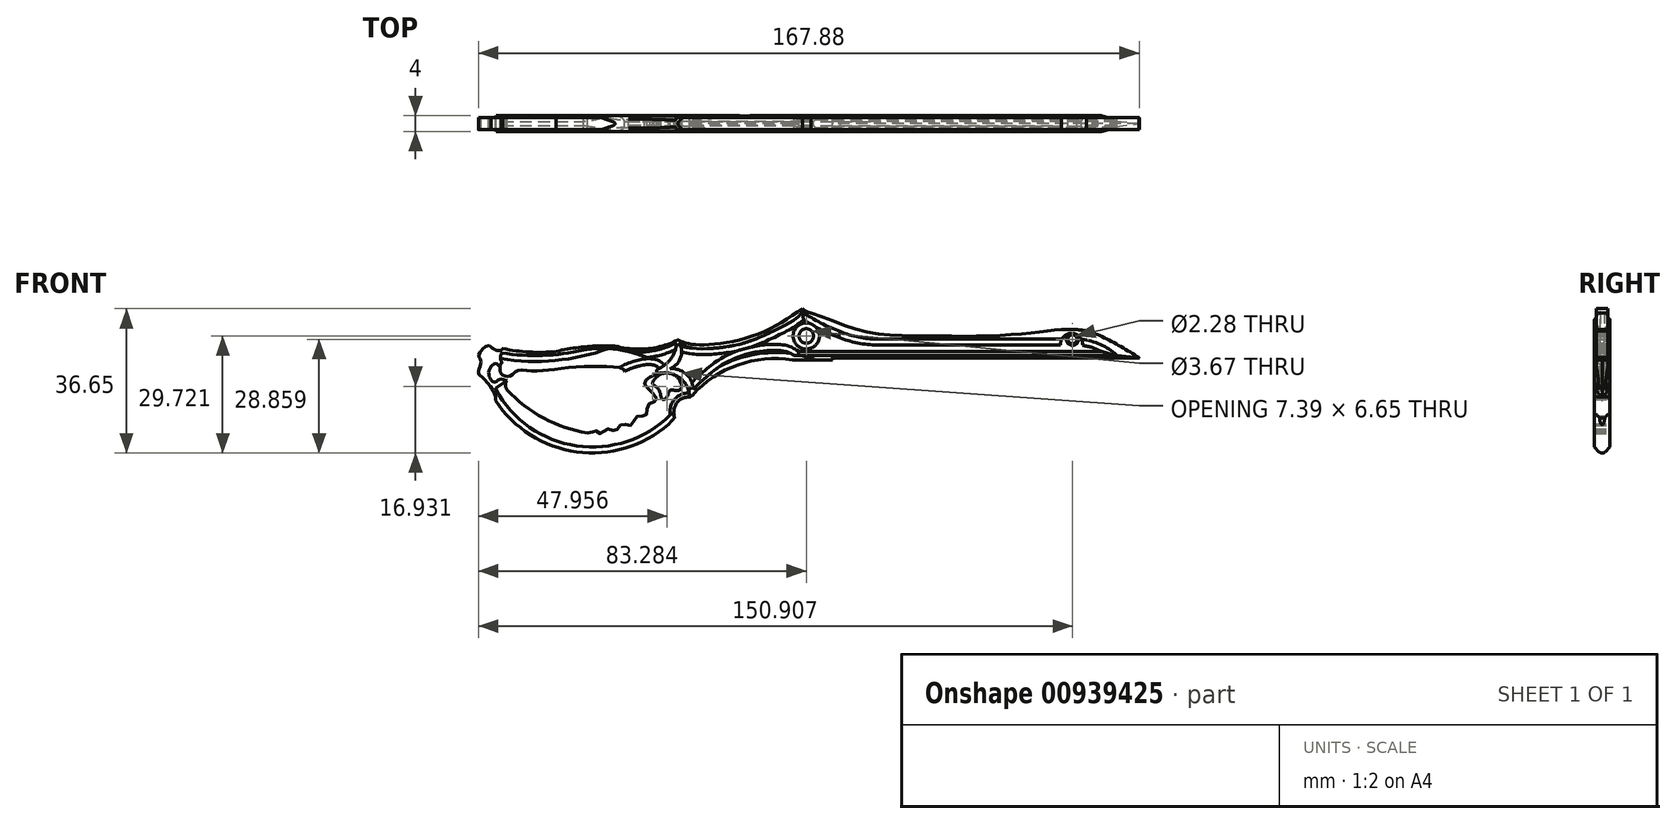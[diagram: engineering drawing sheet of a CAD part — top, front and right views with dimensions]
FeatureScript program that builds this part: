
annotation { "Feature Type Name" : "Feature", "Feature Type Description" : "" }
export const myFeature = defineFeature(function(context is Context, id is Id, definition is map)
    precondition{}
    {
        {
            var Q0;
            Q0=qCreatedBy(makeId("Front.planeOp"),FACE);
            var sketch = newSketch(context, id + "F0", { "sketchPlane" : qUnion([Q0])});
            skLineSegment(sketch, "E0", {"start": v(-6.71, -12.54) * mm, "end": v(71.27, -12.54) * mm});
            skCircle(sketch, "E1", {"center": v(-13.33, -6.93) * mm, "radius": 1.84 * mm});
            skFitSpline(sketch, "E2", {"points": [v(-12.11, -1.12) * mm, v(-13.61, -0.53) * mm, v(-14.23, 0) * mm, v(-14.23, 0) * mm], "startDerivative": vector(-2.76, 0.75) * mm, "endDerivative": vector(0.22, -0.06) * mm});
            skFitSpline(sketch, "E3", {"points": [v(-14.23, 0) * mm, v(-26.09, -6.66) * mm, v(-38.83, -9.19) * mm, v(-43.7, -8.8) * mm, v(-46, -7.9) * mm, v(-48, -6.13) * mm, v(-48.96, -3.93) * mm], "startDerivative": vector(-43.16, -29.04) * mm, "endDerivative": vector(-6.66, 21.05) * mm});
            skLineSegment(sketch, "E4", {"start": v(65.55, -11.87) * mm, "end": v(-6.71, -11.87) * mm});
            skLineSegment(sketch, "E5", {"start": v(65.55, -11.87) * mm, "end": v(71.27, -12.54) * mm});
            skArc(sketch, "E6", {"start": v(51.62, -7.72) * mm, "mid": v(54.08, -9.28) * mm, "end": v(56.59, -7.8) * mm});
            skArc(sketch, "E7", {"start": v(56.59, -7.8) * mm, "mid": v(54.12, -6.27) * mm, "end": v(51.62, -7.72) * mm});
            skArc(sketch, "E8", {"start": v(65.55, -11.87) * mm, "mid": v(61.4, -9.09) * mm, "end": v(56.59, -7.8) * mm});
            skLineSegment(sketch, "E9", {"start": v(4.84, -7.72) * mm, "end": v(51.62, -7.72) * mm});
            skFitSpline(sketch, "E10", {"points": [v(71.2, -12.47) * mm, v(58.32, -5.78) * mm, v(51.1, -5.34) * mm, v(45.14, -5.98) * mm, v(33.56, -6.92) * mm, v(17.3, -6.92) * mm, v(1.97, -5.9) * mm, v(-12.11, -1.12) * mm], "startDerivative": vector(-75.63, 47.6) * mm, "endDerivative": vector(-90.27, 29.28) * mm});
            skArc(sketch, "E11", {"start": v(71.27, -12.54) * mm, "mid": v(62.17, -6.83) * mm, "end": v(51.53, -5.3) * mm});
            skArc(sketch, "E12", {"start": v(-4.67, -5.85) * mm, "mid": v(0, -7.25) * mm, "end": v(4.84, -7.72) * mm});
            skArc(sketch, "E13", {"start": v(-4.67, -5.85) * mm, "mid": v(-6.16, -9.29) * mm, "end": v(-6.71, -13) * mm});
            skCircle(sketch, "E14", {"center": v(-13.33, -6.93) * mm, "radius": 3 * mm});
            skLineSegment(sketch, "E15", {"start": v(-14.23, 0) * mm, "end": v(-14.34, -0.83) * mm});
            skArc(sketch, "E16", {"start": v(-14.34, -0.83) * mm, "mid": v(-9.65, -3.62) * mm, "end": v(-4.67, -5.85) * mm});
            skLineSegment(sketch, "E17", {"start": v(-6.71, -13) * mm, "end": v(-16.86, -13) * mm});
            skArc(sketch, "E18", {"start": v(-16.86, -13) * mm, "mid": v(-16.58, -12.45) * mm, "end": v(-16.49, -11.84) * mm});
            skFitSpline(sketch, "E19", {"points": [v(-16.49, -11.84) * mm, v(-18.47, -10.89) * mm, v(-24.7, -10.8) * mm, v(-32.93, -13.26) * mm, v(-38.38, -17.07) * mm, v(-42.08, -20.53) * mm], "startDerivative": vector(-13.57, 7.8) * mm, "endDerivative": vector(-16.57, -17.02) * mm});
            skPoint(sketch, "E20", {"position": v(-47.93, -15.27) * mm});
            skArc(sketch, "E21", {"start": v(-47.93, -15.27) * mm, "mid": v(-45.1, -11.92) * mm, "end": v(-46.31, -7.7) * mm});
            skArc(sketch, "E22", {"start": v(-42.27, -22) * mm, "mid": v(-43.33, -17.15) * mm, "end": v(-47.93, -15.27) * mm});
            skFitSpline(sketch, "E23", {"points": [v(-14.34, -0.83) * mm, v(-16.03, -2.58) * mm, v(-23.15, -6.4) * mm, v(-30.92, -9.17) * mm, v(-41.48, -10.11) * mm, v(-45.4, -9.05) * mm], "startDerivative": vector(-10.1, -13.37) * mm, "endDerivative": vector(-20.55, 8.32) * mm});
            skFitSpline(sketch, "E24", {"points": [v(-42.36, -10) * mm, v(-43.44, -9.88) * mm, v(-44.44, -9.68) * mm, v(-45.23, -9.5) * mm], "startDerivative": vector(-3.07, 0.24) * mm, "endDerivative": vector(-2.45, 0.6) * mm});
            skLineSegment(sketch, "E25", {"start": v(-6.71, -11.87) * mm, "end": v(-16.49, -11.84) * mm});
            skArc(sketch, "E26", {"start": v(-16.86, -13) * mm, "mid": v(-30.7, -14.28) * mm, "end": v(-42.27, -22) * mm});
            skPoint(sketch, "E27", {"position": v(-90.44, -10.11) * mm});
            skArc(sketch, "E28", {"start": v(-58.53, -9.72) * mm, "mid": v(-52.28, -9.58) * mm, "end": v(-46.31, -7.7) * mm});
            skArc(sketch, "E29", {"start": v(-90.44, -10.11) * mm, "mid": v(-83.7, -11.04) * mm, "end": v(-76.9, -10.87) * mm});
            skArc(sketch, "E30", {"start": v(-90.44, -10.11) * mm, "mid": v(-90.75, -10.64) * mm, "end": v(-90.67, -11.26) * mm});
            skArc(sketch, "E31", {"start": v(-90.67, -11.26) * mm, "mid": v(-80.27, -11.88) * mm, "end": v(-69.94, -10.47) * mm});
            skArc(sketch, "E32", {"start": v(-58.53, -10.87) * mm, "mid": v(-52.52, -10.74) * mm, "end": v(-46.8, -8.86) * mm});
            skArc(sketch, "E33", {"start": v(-50.73, -15.2) * mm, "mid": v(-47.34, -12.15) * mm, "end": v(-46.31, -7.7) * mm});
            skArc(sketch, "E34", {"start": v(-50.73, -15.2) * mm, "mid": v(-51.31, -15.77) * mm, "end": v(-50.86, -16.46) * mm});
            skArc(sketch, "E35", {"start": v(-90.67, -11.26) * mm, "mid": v(-91.02, -12.43) * mm, "end": v(-90.67, -13.6) * mm});
            skLineSegment(sketch, "E36", {"start": v(-42.94, -22.49) * mm, "end": v(-42.27, -22) * mm});
            skPoint(sketch, "E37", {"position": v(-92.52, -22.95) * mm});
            skFitSpline(sketch, "E38", {"points": [v(-90.67, -13.6) * mm, v(-88.53, -14.18) * mm, v(-87.1, -13.28) * mm, v(-85.34, -13.04) * mm, v(-79.56, -13.87) * mm, v(-71.78, -12.97) * mm, v(-65.23, -11.98) * mm, v(-61.23, -11.82) * mm, v(-59.13, -13.12) * mm, v(-52.32, -11.99) * mm, v(-48.92, -13.55) * mm, v(-46.35, -9.28) * mm], "startDerivative": vector(37, -29.54) * mm, "endDerivative": vector(31.14, 31.46) * mm});
            skFitSpline(sketch, "E39", {"points": [v(-50.73, -15.2) * mm, v(-59.56, -15.94) * mm], "startDerivative": vector(-4.3, 5.9) * mm, "endDerivative": vector(-8.43, -4.22) * mm});
            skFitSpline(sketch, "E40", {"points": [v(-59.56, -15.94) * mm, v(-63.38, -14.71) * mm, v(-75.18, -15.14) * mm, v(-82.6, -15.83) * mm, v(-86.83, -15.8) * mm, v(-88.53, -17.16) * mm, v(-89.81, -17.06) * mm, v(-90.91, -16.47) * mm], "startDerivative": vector(-0.92, 20.53) * mm, "endDerivative": vector(-6.34, 15.13) * mm});
            skArc(sketch, "E41", {"start": v(-90.67, -13.6) * mm, "mid": v(-91.16, -15) * mm, "end": v(-90.91, -16.47) * mm});
            skArc(sketch, "E42", {"start": v(-46.35, -9.28) * mm, "mid": v(-46.44, -8.92) * mm, "end": v(-46.8, -8.86) * mm});
            skArc(sketch, "E43", {"start": v(-58.53, -10.87) * mm, "mid": v(-64.22, -10.09) * mm, "end": v(-69.94, -10.47) * mm});
            skArc(sketch, "E44", {"start": v(-58.53, -9.72) * mm, "mid": v(-67.76, -9.55) * mm, "end": v(-76.9, -10.87) * mm});
            skFitSpline(sketch, "E45", {"points": [v(-89.4, -18.28) * mm, v(-91.14, -17.92) * mm, v(-92.48, -18.7) * mm, v(-93.68, -17.64) * mm, v(-93.9, -15.7) * mm, v(-92.6, -14.04) * mm, v(-91.16, -15) * mm], "startDerivative": vector(-14.32, 2.77) * mm, "endDerivative": vector(6.56, -18.2) * mm});
            skArc(sketch, "E46", {"start": v(-42.94, -22.49) * mm, "mid": v(-46.46, -16.98) * mm, "end": v(-52.98, -17.4) * mm});
            skFitSpline(sketch, "E47", {"points": [v(-52.98, -17.4) * mm, v(-54.43, -18.8) * mm, v(-52.7, -21.01) * mm, v(-51.45, -23.34) * mm, v(-53.6, -24.49) * mm, v(-54.04, -27.08) * mm, v(-56.36, -27.4) * mm, v(-57.8, -29.59) * mm, v(-60.18, -29.37) * mm, v(-61.78, -31.07) * mm, v(-64.03, -30.55) * mm, v(-65.67, -31.75) * mm, v(-67.1, -30.95) * mm, v(-68.9, -31.63) * mm], "startDerivative": vector(-16.02, -15.5) * mm, "endDerivative": vector(-36.84, 16.63) * mm});
            skArc(sketch, "E48", {"start": v(-89.34, -20.62) * mm, "mid": v(-80.03, -27.8) * mm, "end": v(-68.9, -31.63) * mm});
            skArc(sketch, "E49", {"start": v(-52.23, -18.52) * mm, "mid": v(-52.33, -19.08) * mm, "end": v(-51.95, -19.5) * mm});
            skArc(sketch, "E50", {"start": v(-50.28, -22.32) * mm, "mid": v(-50.75, -20.7) * mm, "end": v(-51.95, -19.5) * mm});
            skArc(sketch, "E51", {"start": v(-44.96, -19.94) * mm, "mid": v(-48.05, -16.43) * mm, "end": v(-52.23, -18.52) * mm});
            skFitSpline(sketch, "E52", {"points": [v(-44.96, -19.94) * mm, v(-47.73, -20.7) * mm, v(-48.95, -22.74) * mm, v(-50.28, -22.32) * mm], "startDerivative": vector(-4.33, -12.37) * mm, "endDerivative": vector(-2.26, 10.34) * mm});
            skArc(sketch, "E53", {"start": v(-92.3, -23.28) * mm, "mid": v(-71.7, -36.37) * mm, "end": v(-48.3, -29.4) * mm});
            skLineSegment(sketch, "E54", {"start": v(-92.16, -20.16) * mm, "end": v(-92.3, -23.28) * mm});
            skFitSpline(sketch, "E55", {"points": [v(-42.94, -22.49) * mm, v(-46.8, -27.72) * mm], "startDerivative": vector(-7.7, 0.82) * mm, "endDerivative": vector(2.53, -9.45) * mm});
            skLineSegment(sketch, "E56", {"start": v(-46.8, -27.72) * mm, "end": v(-48.3, -29.4) * mm});
            skLineSegment(sketch, "E57", {"start": v(-48.95, -22.74) * mm, "end": v(-49.66, -26.3) * mm});
            skFitSpline(sketch, "E58", {"points": [v(-92.16, -20.16) * mm, v(-78.76, -31.57) * mm, v(-61.25, -33.61) * mm, v(-49.66, -26.3) * mm], "startDerivative": vector(30.49, -37.12) * mm, "endDerivative": vector(21.41, 30.1) * mm});
            skCircle(sketch, "E59", {"center": v(54.3, -7.8) * mm, "radius": 1.14 * mm});
            skArc(sketch, "E60", {"start": v(-89.4, -18.28) * mm, "mid": v(-89.79, -19.46) * mm, "end": v(-89.34, -20.62) * mm});
            skLineSegment(sketch, "E61", {"start": v(-92.16, -20.16) * mm, "end": v(-89.4, -18.28) * mm});
            skFitSpline(sketch, "E62", {"points": [v(-93.37, -9.75) * mm, v(-96.48, -11.66) * mm, v(-96.14, -12.84) * mm, v(-96.16, -14.48) * mm, v(-96.6, -16.4) * mm, v(-95.49, -17.59) * mm, v(-92.28, -22.61) * mm], "startDerivative": vector(-10.84, 18.33) * mm, "endDerivative": vector(-2.51, -11.89) * mm});
            skArc(sketch, "E63", {"start": v(-93.37, -9.75) * mm, "mid": v(-92.17, -10.52) * mm, "end": v(-90.75, -10.64) * mm});
            skSolve(sketch);
        }
        {
            var Q0;
            Q0=makeQuery(id+"F0.imprint","IMPRINT",FACE,{"disambiguationData":[TD([[makeQuery(id+"F0.imprint","IMPRINT",EDGE,{"derivedFrom":sQuery(id+"F0.wireOp",EDGE,"E6")}),-1.0]])]});
            var Q1;
            Q1=makeQuery(id+"F0.imprint","IMPRINT",FACE,{"disambiguationData":[TD([[makeQuery(id+"F0.imprint","IMPRINT",EDGE,{"derivedFrom":sQuery(id+"F0.wireOp",EDGE,"E14")}),-1.0]])]});
            var Q2;
            Q2=makeQuery(id+"F0.imprint","IMPRINT",FACE,{"disambiguationData":[TD([[makeQuery(id+"F0.imprint","IMPRINT",EDGE,{"derivedFrom":sQuery(id+"F0.wireOp",EDGE,"E1")}),-1.0]])]});
            var Q3;
            Q3=makeQuery(id+"F0.imprint","IMPRINT",FACE,{"disambiguationData":[TD([[makeQuery(id+"F0.imprint","IMPRINT",EDGE,{"derivedFrom":sQuery(id+"F0.wireOp",EDGE,"E6")}),1.0]])]});
            var Q4;
            {var subQ8=sQuery(id+"F0.wireOp",EDGE,"E47");Q4=makeQuery(id+"F0.imprint","IMPRINT",FACE,{"disambiguationData":[TD([[makeQuery(id+"F0.imprint","IMPRINT",EDGE,{"derivedFrom":subQ8}),1.0]])]});}
            var Q5;
            Q5=makeQuery(id+"F0.imprint","IMPRINT",FACE,{"disambiguationData":[TD([[makeQuery(id+"F0.imprint","IMPRINT",EDGE,{"derivedFrom":sQuery(id+"F0.wireOp",EDGE,"E31")}),-1.0]])]});
            var Q6;
            {var subQ2=sQuery(id+"F0.wireOp",EDGE,"E38");Q6=makeQuery(id+"F0.imprint","IMPRINT",FACE,{"disambiguationData":[TD([[makeQuery(id+"F0.imprint","IMPRINT",EDGE,{"derivedFrom":subQ2}),-1.0]])]});}
            extrude(context, id + "F1", {"entities" : qUnion([Q0, Q1, Q2, Q3, Q4, Q5, Q6]), "endBound" : BoundingType.SYMMETRIC, "depth" : 4 * mm, "offsetDistance" : 25.4 * mm});
        }
        {
            var Q0;
            Q0=makeQuery(id+"F1.opExtrude","CAP_EDGE",EDGE,{"disambiguationData":[OSD([sQuery(id+"F0.wireOp",EDGE,"E1")])],"isStart":false});
            var Q1;
            Q1=makeQuery(id+"F1.opExtrude","CAP_EDGE",EDGE,{"disambiguationData":[OSD([sQuery(id+"F0.wireOp",EDGE,"E1")])],"isStart":true});
            chamfer(context, id + "F2", {"entities" : qUnion([Q0, Q1]), "chamferType" : ChamferType.OFFSET_ANGLE, "width" : 1.5 * mm, "oppositeDirection" : false, "angle" : 45 * degree, "tangentPropagation" : true});
        }
        {
            var Q0;
            Q0=makeQuery(id+"F1.opExtrude","CAP_EDGE",EDGE,{"disambiguationData":[OSD([sQuery(id+"F0.wireOp",EDGE,"E59")])],"isStart":false});
            var Q1;
            Q1=makeQuery(id+"F1.opExtrude","CAP_EDGE",EDGE,{"disambiguationData":[OSD([sQuery(id+"F0.wireOp",EDGE,"E59")])],"isStart":true});
            chamfer(context, id + "F3", {"entities" : qUnion([Q0, Q1]), "chamferType" : ChamferType.OFFSET_ANGLE, "width" : 0.4 * mm, "oppositeDirection" : false, "angle" : 45 * degree, "tangentPropagation" : true});
        }
        {
            var Q0;
            {var subQ0=sQuery(id+"F0.wireOp",EDGE,"E5");Q0=makeQuery(id+"F0.imprint","IMPRINT",FACE,{"disambiguationData":[TD([[makeQuery(id+"F0.imprint","IMPRINT",EDGE,{"derivedFrom":subQ0}),-1.0]])]});}
            extrude(context, id + "F4", {"entities" : qUnion([Q0]), "operationType" : NewBodyOperationType.ADD, "endBound" : BoundingType.SYMMETRIC, "depth" : 2 * mm, "offsetDistance" : 25.4 * mm});
        }
        {
            var Q0;
            Q0=makeQuery(id+"F0.imprint","IMPRINT",FACE,{"disambiguationData":[TD([[makeQuery(id+"F0.imprint","IMPRINT",EDGE,{"derivedFrom":sQuery(id+"F0.wireOp",EDGE,"E18")}),1.0]])]});
            var Q1;
            {var subQ0=sQuery(id+"F0.wireOp",EDGE,"E17");Q1=makeQuery(id+"F0.imprint","IMPRINT",FACE,{"disambiguationData":[TD([[makeQuery(id+"F0.imprint","IMPRINT",EDGE,{"derivedFrom":subQ0}),-1.0]])]});}
            var Q2;
            Q2=makeQuery(id+"F0.imprint","IMPRINT",FACE,{"disambiguationData":[TD([[makeQuery(id+"F0.imprint","IMPRINT",EDGE,{"derivedFrom":sQuery(id+"F0.wireOp",EDGE,"E5")}),1.0]])]});
            var Q3;
            {var subQ0=sQuery(id+"F0.wireOp",EDGE,"E23");Q3=makeQuery(id+"F0.imprint","IMPRINT",FACE,{"disambiguationData":[TD([[makeQuery(id+"F0.imprint","IMPRINT",EDGE,{"derivedFrom":subQ0}),-1.0]])]});}
            var Q4;
            {var subQ4=sQuery(id+"F0.wireOp",EDGE,"E34");Q4=makeQuery(id+"F0.imprint","IMPRINT",FACE,{"disambiguationData":[TD([[makeQuery(id+"F0.imprint","IMPRINT",EDGE,{"derivedFrom":subQ4}),1.0]])]});}
            var Q5;
            Q5=makeQuery(id+"F0.imprint","IMPRINT",FACE,{"disambiguationData":[TD([[makeQuery(id+"F0.imprint","IMPRINT",EDGE,{"derivedFrom":sQuery(id+"F0.wireOp",EDGE,"E49")}),1.0]])]});
            var Q6;
            {var subQ4=sQuery(id+"F0.wireOp",EDGE,"E28");Q6=makeQuery(id+"F0.imprint","IMPRINT",FACE,{"disambiguationData":[TD([[makeQuery(id+"F0.imprint","IMPRINT",EDGE,{"derivedFrom":subQ4}),-1.0]])]});}
            var Q7;
            {var subQ1=sQuery(id+"F0.wireOp",EDGE,"E35");Q7=makeQuery(id+"F0.imprint","IMPRINT",FACE,{"disambiguationData":[TD([[makeQuery(id+"F0.imprint","IMPRINT",EDGE,{"derivedFrom":subQ1}),-1.0]])]});}
            extrude(context, id + "F5", {"entities" : qUnion([Q0, Q1, Q2, Q3, Q4, Q5, Q6, Q7]), "endBound" : BoundingType.SYMMETRIC, "depth" : 3 * mm, "offsetDistance" : 25.4 * mm});
        }
        {
            var Q0;
            Q0=makeQuery(id+"F5.opExtrude","CAP_EDGE",EDGE,{"disambiguationData":[OSD([sQuery(id+"F0.wireOp",EDGE,"E10")])],"isStart":false});
            var Q1;
            Q1=makeQuery(id+"F5.opExtrude","CAP_EDGE",EDGE,{"disambiguationData":[OSD([sQuery(id+"F0.wireOp",EDGE,"E11")])],"isStart":false});
            var Q2;
            Q2=makeQuery(id+"F1.opExtrude","CAP_EDGE",EDGE,{"disambiguationData":[OSD([sQuery(id+"F0.wireOp",EDGE,"E9")])],"isStart":false});
            var Q3;
            Q3=makeQuery(id+"F1.opExtrude","CAP_EDGE",EDGE,{"disambiguationData":[OSD([sQuery(id+"F0.wireOp",EDGE,"E8")])],"isStart":false});
            var Q4;
            Q4=makeQuery(id+"F1.opExtrude","CAP_EDGE",EDGE,{"disambiguationData":[OSD([sQuery(id+"F0.wireOp",EDGE,"E23")])],"isStart":false});
            var Q5;
            Q5=makeQuery(id+"F5.opExtrude","CAP_EDGE",EDGE,{"disambiguationData":[OSD([sQuery(id+"F0.wireOp",EDGE,"E10")])],"isStart":true});
            var Q6;
            Q6=makeQuery(id+"F5.opExtrude","CAP_EDGE",EDGE,{"disambiguationData":[OSD([sQuery(id+"F0.wireOp",EDGE,"E11")])],"isStart":true});
            var Q7;
            Q7=makeQuery(id+"F1.opExtrude","CAP_EDGE",EDGE,{"disambiguationData":[OSD([sQuery(id+"F0.wireOp",EDGE,"E9")])],"isStart":true});
            var Q8;
            Q8=makeQuery(id+"F1.opExtrude","CAP_EDGE",EDGE,{"disambiguationData":[OSD([sQuery(id+"F0.wireOp",EDGE,"E8")])],"isStart":true});
            var Q9;
            Q9=makeQuery(id+"F1.opExtrude","CAP_EDGE",EDGE,{"disambiguationData":[OSD([sQuery(id+"F0.wireOp",EDGE,"E23")])],"isStart":true});
            var Q10;
            Q10=makeQuery(id+"F5.opExtrude","CAP_EDGE",EDGE,{"disambiguationData":[OSD([sQuery(id+"F0.wireOp",EDGE,"E3")])],"isStart":true});
            var Q11;
            Q11=makeQuery(id+"F5.opExtrude","CAP_EDGE",EDGE,{"disambiguationData":[OSD([sQuery(id+"F0.wireOp",EDGE,"E3")])],"isStart":false});
            chamfer(context, id + "F6", {"entities" : qUnion([Q0, Q1, Q2, Q3, Q4, Q5, Q6, Q7, Q8, Q9, Q10, Q11]), "chamferType" : ChamferType.OFFSET_ANGLE, "width" : 1.5 * mm, "oppositeDirection" : false, "angle" : 45 * degree, "tangentPropagation" : true});
        }
        {
            var Q0;
            Q0=makeQuery(id+"F1.opExtrude","CAP_EDGE",EDGE,{"disambiguationData":[OSD([sQuery(id+"F0.wireOp",EDGE,"E19")])],"isStart":false});
            var Q1;
            Q1=makeQuery(id+"F5.opExtrude","CAP_EDGE",EDGE,{"disambiguationData":[OSD([sQuery(id+"F0.wireOp",EDGE,"E26")])],"isStart":false});
            var Q2;
            Q2=makeQuery(id+"F5.opExtrude","CAP_EDGE",EDGE,{"disambiguationData":[OSD([sQuery(id+"F0.wireOp",EDGE,"E26")])],"isStart":true});
            var Q3;
            Q3=makeQuery(id+"F1.opExtrude","CAP_EDGE",EDGE,{"disambiguationData":[OSD([sQuery(id+"F0.wireOp",EDGE,"E19")])],"isStart":true});
            var Q4;
            Q4=makeQuery(id+"F1.opExtrude","CAP_EDGE",EDGE,{"disambiguationData":[OSD([sQuery(id+"F0.wireOp",EDGE,"E53")])],"isStart":false});
            var Q5;
            Q5=makeQuery(id+"F1.opExtrude","CAP_EDGE",EDGE,{"disambiguationData":[OSD([sQuery(id+"F0.wireOp",EDGE,"E53")])],"isStart":true});
            var Q6;
            Q6=makeQuery(id+"F1.opExtrude","CAP_EDGE",EDGE,{"disambiguationData":[OSD([sQuery(id+"F0.wireOp",EDGE,"E39")])],"isStart":true});
            var Q7;
            Q7=makeQuery(id+"F1.opExtrude","CAP_EDGE",EDGE,{"disambiguationData":[OSD([sQuery(id+"F0.wireOp",EDGE,"E39")])],"isStart":false});
            chamfer(context, id + "F7", {"entities" : qUnion([Q0, Q1, Q2, Q3, Q4, Q5, Q6, Q7]), "chamferType" : ChamferType.OFFSET_ANGLE, "width" : 1.5 * mm, "oppositeDirection" : false, "angle" : 45 * degree, "tangentPropagation" : true});
        }
        {
            var Q0;
            Q0=makeQuery(id+"F1.opExtrude","CAP_EDGE",EDGE,{"disambiguationData":[OSD([sQuery(id+"F0.wireOp",EDGE,"E31")])],"isStart":true});
            var Q1;
            Q1=makeQuery(id+"F1.opExtrude","CAP_EDGE",EDGE,{"disambiguationData":[OSD([sQuery(id+"F0.wireOp",EDGE,"E32")])],"isStart":true});
            var Q2;
            Q2=makeQuery(id+"F1.opExtrude","CAP_EDGE",EDGE,{"disambiguationData":[OSD([sQuery(id+"F0.wireOp",EDGE,"E32")])],"isStart":false});
            var Q3;
            Q3=makeQuery(id+"F1.opExtrude","CAP_EDGE",EDGE,{"disambiguationData":[OSD([sQuery(id+"F0.wireOp",EDGE,"E31")])],"isStart":false});
            var Q4;
            Q4=makeQuery(id+"F5.opExtrude","CAP_EDGE",EDGE,{"disambiguationData":[OSD([sQuery(id+"F0.wireOp",EDGE,"E28")])],"isStart":false});
            var Q5;
            Q5=makeQuery(id+"F5.opExtrude","CAP_EDGE",EDGE,{"disambiguationData":[OSD([sQuery(id+"F0.wireOp",EDGE,"E28")])],"isStart":true});
            chamfer(context, id + "F8", {"entities" : qUnion([Q0, Q1, Q2, Q3, Q4, Q5]), "chamferType" : ChamferType.OFFSET_ANGLE, "width" : 1.5 * mm, "oppositeDirection" : false, "angle" : 45 * degree, "tangentPropagation" : true});
        }
        {
            var Q0;
            {var subQ0=sQuery(id+"F0.wireOp",EDGE,"E28");Q0=makeQuery(id+"F8.opChamfer","BLEND_EDGE",EDGE,{"blendedFrom":[makeQuery(id+"F5.opExtrude","CAP_EDGE",EDGE,{"disambiguationData":[OSD([subQ0])],"isStart":true}),makeQuery(id+"F5.opExtrude","CAP_EDGE",EDGE,{"disambiguationData":[OSD([subQ0])],"isStart":false})],"blendedInto":[]});}
            var Q1;
            {var subQ0=sQuery(id+"F0.wireOp",EDGE,"E53");Q1=makeQuery(id+"F7.opChamfer","BLEND_EDGE",EDGE,{"blendedFrom":[makeQuery(id+"F1.opExtrude","CAP_EDGE",EDGE,{"disambiguationData":[OSD([subQ0])],"isStart":false}),makeQuery(id+"F1.opExtrude","SWEPT_FACE",FACE,{"disambiguationData":[OSD([subQ0])]})],"blendedInto":[makeQuery(id+"F1.opExtrude","SWEPT_FACE",FACE,{"disambiguationData":[OSD([subQ0])]})]});}
            var Q2;
            {var subQ0=sQuery(id+"F0.wireOp",EDGE,"E53");Q2=makeQuery(id+"F7.opChamfer","BLEND_EDGE",EDGE,{"blendedFrom":[makeQuery(id+"F1.opExtrude","CAP_EDGE",EDGE,{"disambiguationData":[OSD([subQ0])],"isStart":true}),makeQuery(id+"F1.opExtrude","SWEPT_FACE",FACE,{"disambiguationData":[OSD([subQ0])]})],"blendedInto":[makeQuery(id+"F1.opExtrude","SWEPT_FACE",FACE,{"disambiguationData":[OSD([subQ0])]})]});}
            var Q3;
            Q3=makeQuery(id+"F1.opExtrude","CAP_EDGE",EDGE,{"disambiguationData":[OSD([sQuery(id+"F0.wireOp",EDGE,"E55")])],"isStart":false});
            var Q4;
            Q4=makeQuery(id+"F1.opExtrude","CAP_EDGE",EDGE,{"disambiguationData":[OSD([sQuery(id+"F0.wireOp",EDGE,"E55")])],"isStart":true});
            fillet(context, id + "F9", {"entities" : qUnion([Q0, Q1, Q2, Q3, Q4]), "radius" : 1 * mm, "tangentPropagation" : true, "allowEdgeOverflow" : false});
        }
        {
            var Q0;
            Q0=makeQuery(id+"F1.opExtrude","CAP_EDGE",EDGE,{"disambiguationData":[OSD([sQuery(id+"F0.wireOp",EDGE,"E4")])],"isStart":true});
            var Q1;
            Q1=makeQuery(id+"F1.opExtrude","CAP_EDGE",EDGE,{"disambiguationData":[OSD([sQuery(id+"F0.wireOp",EDGE,"E4")])],"isStart":false});
            var Q2;
            Q2=makeQuery(id+"F4.opExtrude","CAP_EDGE",EDGE,{"disambiguationData":[OSD([sQuery(id+"F0.wireOp",EDGE,"E0")])],"isStart":false});
            var Q3;
            Q3=makeQuery(id+"F4.opExtrude","CAP_EDGE",EDGE,{"disambiguationData":[OSD([sQuery(id+"F0.wireOp",EDGE,"E0")])],"isStart":true});
            chamfer(context, id + "F10", {"entities" : qUnion([Q0, Q1, Q2, Q3]), "chamferType" : ChamferType.OFFSET_ANGLE, "width" : 1 * mm, "oppositeDirection" : false, "angle" : 45 * degree, "tangentPropagation" : true});
        }
    });
